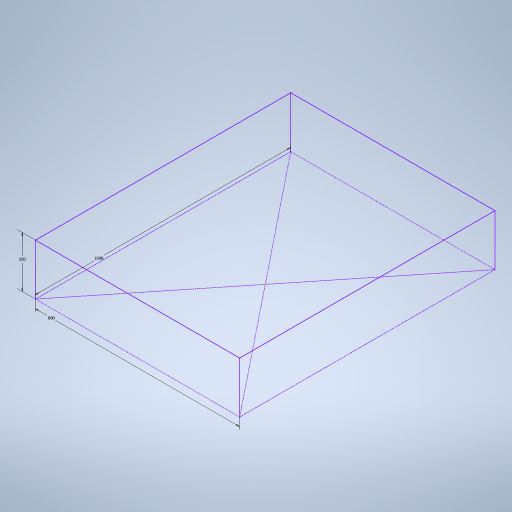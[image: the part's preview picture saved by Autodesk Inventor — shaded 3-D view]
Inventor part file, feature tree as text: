
AUTODESK INVENTOR PART (.ipt)
format: ipt  version: 2024.2 (Build 282272000, 272)  size: 244,224 bytes
history: native  units: in
note: dims shown in document units (in); Inventor stores cm internally (conversion verified against a paired STEP export)
features: sketch x2
ambient origin geometry x8: Origin, YZ Plane, XZ Plane, XY Plane, X Axis, Y Axis, Z Axis, Center Point
feature tree (2):
  sketch  "Sketch3"  dims[d4=39.3701in d5=31.4961in d6=7.874in]
  sketch  "3D Sketch3"
